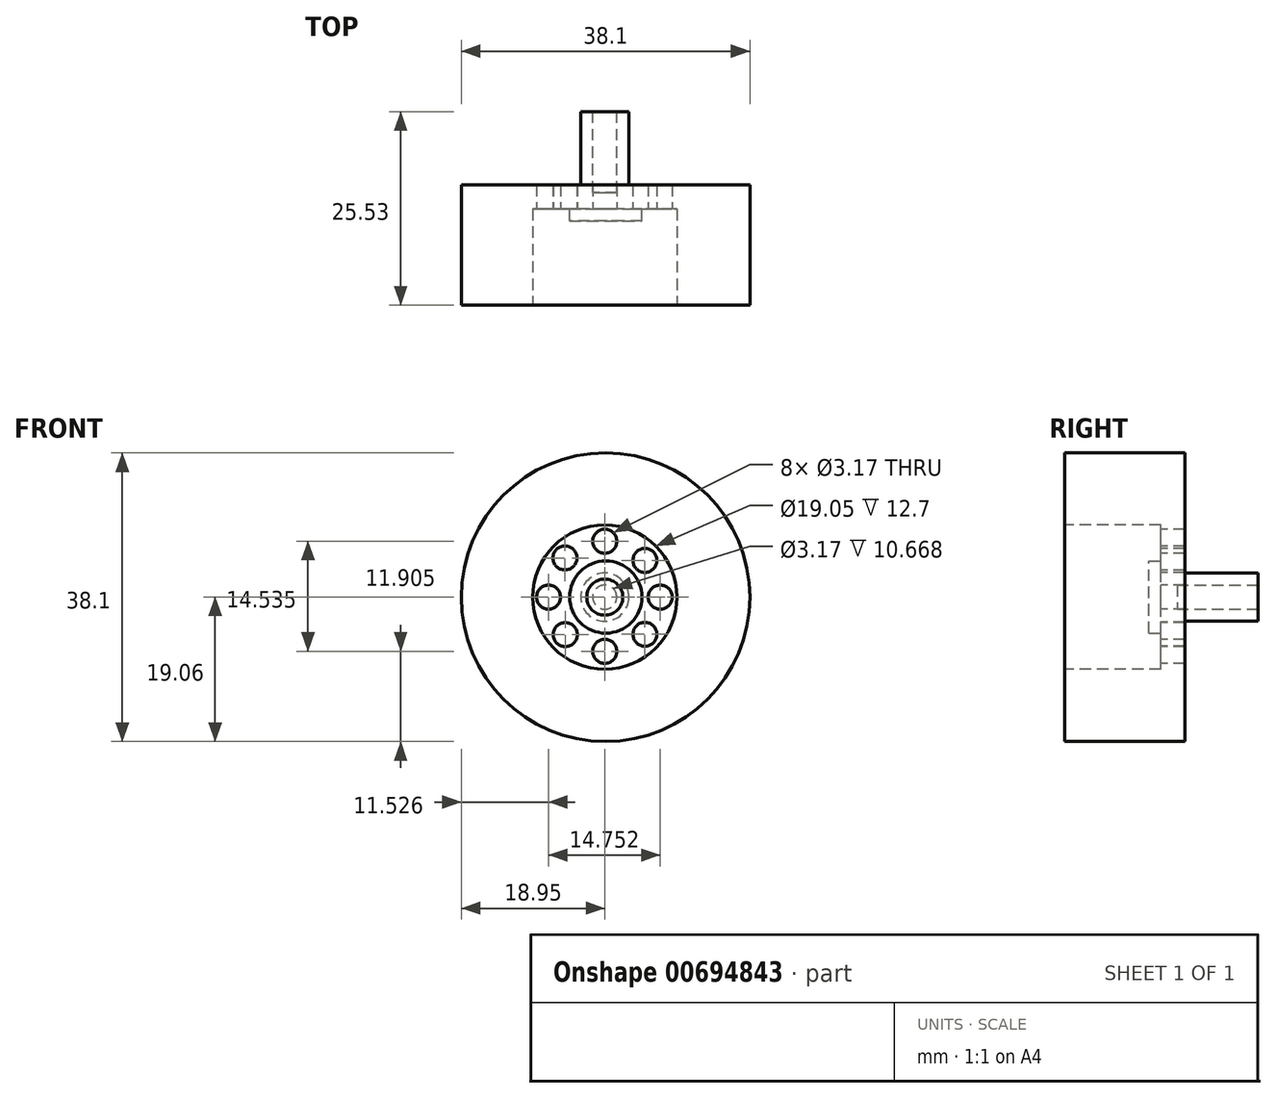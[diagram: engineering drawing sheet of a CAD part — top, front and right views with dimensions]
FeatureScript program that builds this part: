
annotation { "Feature Type Name" : "Feature", "Feature Type Description" : "" }
export const myFeature = defineFeature(function(context is Context, id is Id, definition is map)
    precondition{}
    {
        {
            var Q0;
            Q0=qCreatedBy(makeId("Front.planeOp"),FACE);
            var sketch = newSketch(context, id + "F0", { "sketchPlane" : qUnion([Q0])});
            skCircle(sketch, "E0", {"center": v(0.1, -0.01) * mm, "radius": 19.05 * mm});
            skSolve(sketch);
        }
        {
            var Q0;
            Q0 = qSketchRegion(id + "F0", true);
            extrude(context, id + "F1", {"entities" : qUnion([Q0]), "depth" : 15.88 * mm, "offsetDistance" : 25.4 * mm});
        }
        {
            var Q0;
            Q0=makeQuery(id+"F1.opExtrude","CAP_FACE",FACE,{"disambiguationData":[OSD([sQuery(id+"F0.wireOp",EDGE,"E0")])],"isStart":false});
            var sketch = newSketch(context, id + "F2", { "sketchPlane" : qUnion([Q0])});
            skCircle(sketch, "E1", {"center": v(0, 0) * mm, "radius": 9.53 * mm});
            skSolve(sketch);
        }
        {
            var Q0;
            Q0 = qSketchRegion(id + "F2", true);
            extrude(context, id + "F3", {"entities" : qUnion([Q0]), "operationType" : NewBodyOperationType.REMOVE, "oppositeDirection" : true, "depth" : 12.7 * mm, "offsetDistance" : 25.4 * mm});
        }
        {
            var Q0;
            Q0=makeQuery(id+"F3.boolean.opBoolean","COPY",FACE,{"derivedFrom":makeQuery(id+"F3.opExtrude","CAP_FACE",FACE,{"disambiguationData":[OSD([sQuery(id+"F2.wireOp",EDGE,"E1")])],"isStart":false})});
            var sketch = newSketch(context, id + "F4", { "sketchPlane" : qUnion([Q0])});
            skCircle(sketch, "E2", {"center": v(0, 7.38) * mm, "radius": 1.59 * mm});
            skSolve(sketch);
        }
        {
            var Q0;
            Q0 = qSketchRegion(id + "F4", true);
            extrude(context, id + "F5", {"entities" : qUnion([Q0]), "operationType" : NewBodyOperationType.REMOVE, "oppositeDirection" : true, "depth" : 25.4 * mm, "offsetDistance" : 25.4 * mm});
        }
        {
            var Q0;
            Q0=makeQuery(id+"F3.boolean.opBoolean","COPY",FACE,{"derivedFrom":makeQuery(id+"F3.opExtrude","CAP_FACE",FACE,{"disambiguationData":[OSD([sQuery(id+"F2.wireOp",EDGE,"E1")])],"isStart":false})});
            var sketch = newSketch(context, id + "F6", { "sketchPlane" : qUnion([Q0])});
            skCircle(sketch, "E3", {"center": v(0, -7.15) * mm, "radius": 1.59 * mm});
            skSolve(sketch);
        }
        {
            var Q0;
            Q0 = qSketchRegion(id + "F6", true);
            extrude(context, id + "F7", {"entities" : qUnion([Q0]), "operationType" : NewBodyOperationType.REMOVE, "oppositeDirection" : true, "depth" : 25.4 * mm, "offsetDistance" : 25.4 * mm});
        }
        {
            var Q0;
            Q0=makeQuery(id+"F3.boolean.opBoolean","COPY",FACE,{"derivedFrom":makeQuery(id+"F3.opExtrude","CAP_FACE",FACE,{"disambiguationData":[OSD([sQuery(id+"F2.wireOp",EDGE,"E1")])],"isStart":false})});
            var sketch = newSketch(context, id + "F8", { "sketchPlane" : qUnion([Q0])});
            skCircle(sketch, "E4", {"center": v(7.33, 0) * mm, "radius": 1.59 * mm});
            skSolve(sketch);
        }
        {
            var Q0;
            Q0 = qSketchRegion(id + "F8", true);
            extrude(context, id + "F9", {"entities" : qUnion([Q0]), "operationType" : NewBodyOperationType.REMOVE, "oppositeDirection" : true, "depth" : 25.4 * mm, "offsetDistance" : 25.4 * mm});
        }
        {
            var Q0;
            Q0=makeQuery(id+"F3.boolean.opBoolean","COPY",FACE,{"derivedFrom":makeQuery(id+"F3.opExtrude","CAP_FACE",FACE,{"disambiguationData":[OSD([sQuery(id+"F2.wireOp",EDGE,"E1")])],"isStart":false})});
            var sketch = newSketch(context, id + "F10", { "sketchPlane" : qUnion([Q0])});
            skCircle(sketch, "E5", {"center": v(-7.42, 0) * mm, "radius": 1.59 * mm});
            skSolve(sketch);
        }
        {
            var Q0;
            Q0 = qSketchRegion(id + "F10", true);
            extrude(context, id + "F11", {"entities" : qUnion([Q0]), "operationType" : NewBodyOperationType.REMOVE, "oppositeDirection" : true, "depth" : 25.4 * mm, "offsetDistance" : 25.4 * mm});
        }
        {
            var Q0;
            Q0=makeQuery(id+"F3.boolean.opBoolean","COPY",FACE,{"derivedFrom":makeQuery(id+"F3.opExtrude","CAP_FACE",FACE,{"disambiguationData":[OSD([sQuery(id+"F2.wireOp",EDGE,"E1")])],"isStart":false})});
            var sketch = newSketch(context, id + "F12", { "sketchPlane" : qUnion([Q0])});
            skCircle(sketch, "E6", {"center": v(-5.25, 5.17) * mm, "radius": 1.59 * mm});
            skSolve(sketch);
        }
        {
            var Q0;
            Q0 = qSketchRegion(id + "F12", true);
            extrude(context, id + "F13", {"entities" : qUnion([Q0]), "operationType" : NewBodyOperationType.REMOVE, "oppositeDirection" : true, "depth" : 25.4 * mm, "offsetDistance" : 25.4 * mm});
        }
        {
            var Q0;
            Q0=makeQuery(id+"F3.boolean.opBoolean","COPY",FACE,{"derivedFrom":makeQuery(id+"F3.opExtrude","CAP_FACE",FACE,{"disambiguationData":[OSD([sQuery(id+"F2.wireOp",EDGE,"E1")])],"isStart":false})});
            var sketch = newSketch(context, id + "F14", { "sketchPlane" : qUnion([Q0])});
            skCircle(sketch, "E7", {"center": v(5.3, 4.85) * mm, "radius": 1.59 * mm});
            skSolve(sketch);
        }
        {
            var Q0;
            Q0 = qSketchRegion(id + "F14", true);
            extrude(context, id + "F15", {"entities" : qUnion([Q0]), "operationType" : NewBodyOperationType.REMOVE, "oppositeDirection" : true, "depth" : 25.4 * mm, "offsetDistance" : 25.4 * mm});
        }
        {
            var Q0;
            Q0=makeQuery(id+"F3.boolean.opBoolean","COPY",FACE,{"derivedFrom":makeQuery(id+"F3.opExtrude","CAP_FACE",FACE,{"disambiguationData":[OSD([sQuery(id+"F2.wireOp",EDGE,"E1")])],"isStart":false})});
            var sketch = newSketch(context, id + "F16", { "sketchPlane" : qUnion([Q0])});
            skCircle(sketch, "E8", {"center": v(-5.22, -4.95) * mm, "radius": 1.59 * mm});
            skSolve(sketch);
        }
        {
            var Q0;
            Q0 = qSketchRegion(id + "F16", true);
            extrude(context, id + "F17", {"entities" : qUnion([Q0]), "operationType" : NewBodyOperationType.REMOVE, "oppositeDirection" : true, "depth" : 25.4 * mm, "offsetDistance" : 25.4 * mm});
        }
        {
            var Q0;
            Q0=makeQuery(id+"F3.boolean.opBoolean","COPY",FACE,{"derivedFrom":makeQuery(id+"F3.opExtrude","CAP_FACE",FACE,{"disambiguationData":[OSD([sQuery(id+"F2.wireOp",EDGE,"E1")])],"isStart":false})});
            var sketch = newSketch(context, id + "F18", { "sketchPlane" : qUnion([Q0])});
            skCircle(sketch, "E9", {"center": v(5.3, -4.91) * mm, "radius": 1.59 * mm});
            skSolve(sketch);
        }
        {
            var Q0;
            Q0 = qSketchRegion(id + "F18", true);
            extrude(context, id + "F19", {"entities" : qUnion([Q0]), "operationType" : NewBodyOperationType.REMOVE, "oppositeDirection" : true, "depth" : 25.4 * mm, "offsetDistance" : 25.4 * mm});
        }
        {
            var Q0;
            Q0=makeQuery(id+"F3.boolean.opBoolean","COPY",FACE,{"derivedFrom":makeQuery(id+"F3.opExtrude","CAP_FACE",FACE,{"disambiguationData":[OSD([sQuery(id+"F2.wireOp",EDGE,"E1")])],"isStart":false})});
            var sketch = newSketch(context, id + "F20", { "sketchPlane" : qUnion([Q0])});
            skCircle(sketch, "E10", {"center": v(0.14, 0.01) * mm, "radius": 4.76 * mm});
            skSolve(sketch);
        }
        {
            var Q0;
            Q0 = qSketchRegion(id + "F20", true);
            extrude(context, id + "F21", {"entities" : qUnion([Q0]), "operationType" : NewBodyOperationType.ADD, "depth" : 1.59 * mm, "offsetDistance" : 25.4 * mm});
        }
        {
            var Q0;
            Q0=makeQuery(id+"F21.opExtrude","CAP_FACE",FACE,{"disambiguationData":[OSD([sQuery(id+"F20.wireOp",EDGE,"E10")])],"isStart":false});
            var sketch = newSketch(context, id + "F22", { "sketchPlane" : qUnion([Q0])});
            skCircle(sketch, "E11", {"center": v(0, 0) * mm, "radius": 2.38 * mm});
            skSolve(sketch);
        }
        {
            var Q0;
            Q0 = qSketchRegion(id + "F22", true);
            extrude(context, id + "F23", {"entities" : qUnion([Q0]), "operationType" : NewBodyOperationType.ADD, "depth" : 1 / 406.4 * mm, "offsetDistance" : 25.4 * mm});
        }
        {
            var Q0;
            Q0=makeQuery(id+"F1.opExtrude","CAP_FACE",FACE,{"disambiguationData":[OSD([sQuery(id+"F0.wireOp",EDGE,"E0")])],"isStart":true});
            var sketch = newSketch(context, id + "F24", { "sketchPlane" : qUnion([Q0])});
            skCircle(sketch, "E12", {"center": v(0, 0) * mm, "radius": 3.18 * mm});
            skSolve(sketch);
        }
        {
            var Q0;
            Q0 = qSketchRegion(id + "F24", true);
            extrude(context, id + "F25", {"entities" : qUnion([Q0]), "operationType" : NewBodyOperationType.ADD, "depth" : 9.65 * mm, "offsetDistance" : 25.4 * mm});
        }
        {
            var Q0;
            Q0=makeQuery(id+"F25.opExtrude","CAP_FACE",FACE,{"disambiguationData":[OSD([sQuery(id+"F24.wireOp",EDGE,"E12")])],"isStart":false});
            var sketch = newSketch(context, id + "F26", { "sketchPlane" : qUnion([Q0])});
            skCircle(sketch, "E13", {"center": v(0, 0) * mm, "radius": 1.59 * mm});
            skSolve(sketch);
        }
        {
            var Q0;
            Q0 = qSketchRegion(id + "F26", true);
            extrude(context, id + "F27", {"entities" : qUnion([Q0]), "operationType" : NewBodyOperationType.REMOVE, "oppositeDirection" : true, "depth" : 10.67 * mm, "offsetDistance" : 25.4 * mm});
        }
    });
